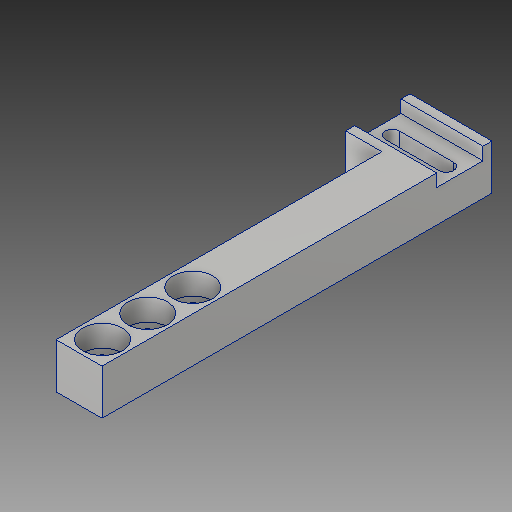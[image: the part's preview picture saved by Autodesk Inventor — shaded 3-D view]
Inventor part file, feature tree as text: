
AUTODESK INVENTOR PART (.ipt)
format: ipt  version: 2019 (Build 230136000, 136)  size: 161,792 bytes
history: native  units: mm
features: extrude x5, sketch x4, mirror x1
ambient origin geometry x8: Origin, YZ Plane, XZ Plane, XY Plane, X Axis, Y Axis, Z Axis, Center Point
bodies: Solid1 (feature_tree)
feature tree (10):
  extrude  "Extrusion1"  Depth=108.0mm
  extrude  "Extrusion2"  Depth=90.2mm
  extrude  "Extrusion3"  Depth=12.8mm
  sketch  "Sketch4"  dims[d7=3.5mm d8=0.0mm d9=4.0mm d10=4.0mm d11=3.5mm d12=0.0mm d13=11.0mm d14=11.0mm d15=11.0mm d16=12.5mm d17=12.5mm d18=6.5mm d19=6.5mm d20=6.5mm d21=3.5mm d22=0.0mm d23=6.0mm d24=0.0mm d25=6.5mm d26=15.0mm d27=4.0mm]
  extrude  "Extrusion4"  Depth=4.0mm
  extrude  "Extrusion5"  Depth=4.0mm
  mirror  "Mirror1"
  sketch  "Sketch1"  dims[d0=22.7mm d1=108.0mm]
  sketch  "Sketch2"  dims[d2=12.7mm d3=90.2mm]
  sketch  "Sketch3"  dims[d4=12.5mm d5=0.0mm d6=12.8mm]
